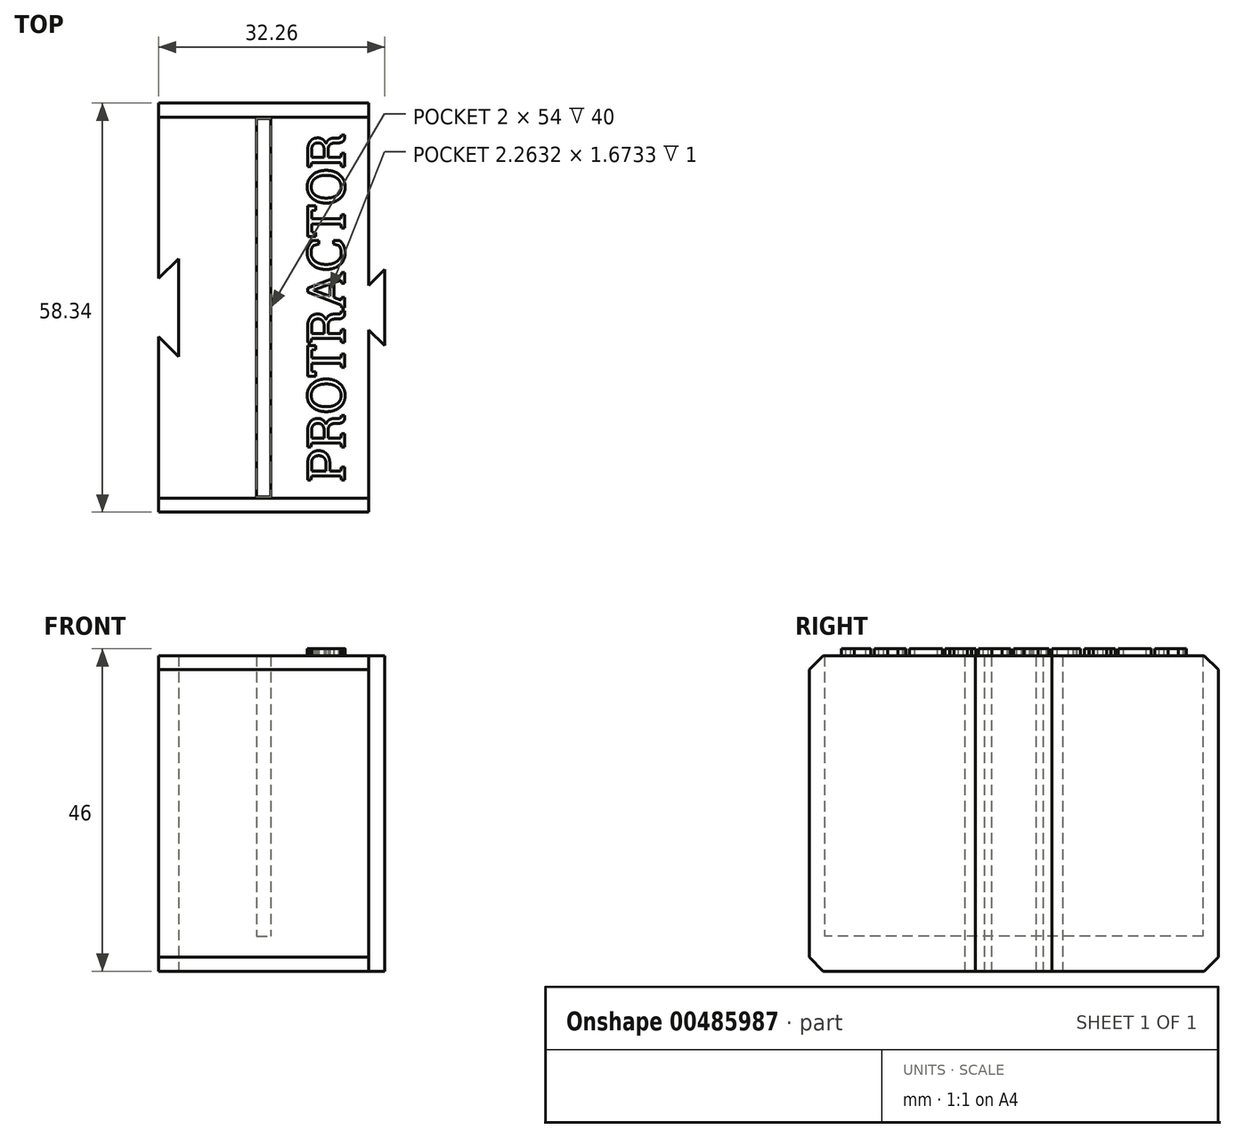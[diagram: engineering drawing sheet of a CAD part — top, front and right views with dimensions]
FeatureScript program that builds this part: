
annotation { "Feature Type Name" : "Feature", "Feature Type Description" : "" }
export const myFeature = defineFeature(function(context is Context, id is Id, definition is map)
    precondition{}
    {
        {
            var Q0;
            Q0=qCreatedBy(makeId("Top.planeOp"),FACE);
            var sketch = newSketch(context, id + "F0", { "sketchPlane" : qUnion([Q0])});
            skLineSegment(sketch, "E0", {"start": v(-15, 4.17) * mm, "end": v(-15, 29.17) * mm});
            skLineSegment(sketch, "E1", {"start": v(-15, 29.17) * mm, "end": v(15, 29.17) * mm});
            skLineSegment(sketch, "E2", {"start": v(15, 29.17) * mm, "end": v(15, 3.17) * mm});
            skLineSegment(sketch, "E3", {"start": v(-15, 4.17) * mm, "end": v(-12.17, 7) * mm});
            skLineSegment(sketch, "E4", {"start": v(-12.17, 7) * mm, "end": v(-12.17, 0) * mm});
            skLineSegment(sketch, "E5", {"start": v(15, 3.17) * mm, "end": v(17.26, 5.43) * mm});
            skLineSegment(sketch, "E6", {"start": v(17.26, 5.43) * mm, "end": v(17.26, -0.57) * mm});
            skLineSegment(sketch, "E7.MirrorCS", {"start": v(-15, -4.17) * mm, "end": v(-12.17, -7) * mm});
            skLineSegment(sketch, "E8.MirrorCS", {"start": v(15, -29.17) * mm, "end": v(15, -3.17) * mm});
            skLineSegment(sketch, "E9.MirrorCS", {"start": v(-12.17, -7) * mm, "end": v(-12.17, 0) * mm});
            skLineSegment(sketch, "E10.MirrorCS", {"start": v(-15, -4.17) * mm, "end": v(-15, -29.17) * mm});
            skLineSegment(sketch, "E11.MirrorCS", {"start": v(17.26, -5.43) * mm, "end": v(17.26, 0.57) * mm});
            skLineSegment(sketch, "E12.MirrorCS", {"start": v(15, -3.17) * mm, "end": v(17.26, -5.43) * mm});
            skLineSegment(sketch, "E13.MirrorCS", {"start": v(-15, -29.17) * mm, "end": v(15, -29.17) * mm});
            skLineSegment(sketch, "E14.bottom", {"start": v(-1, 27) * mm, "end": v(1, 27) * mm});
            skLineSegment(sketch, "E14.top", {"start": v(-1, -27) * mm, "end": v(1, -27) * mm});
            skLineSegment(sketch, "E14.left", {"start": v(-1, 27) * mm, "end": v(-1, -27) * mm});
            skLineSegment(sketch, "E14.right", {"start": v(1, 27) * mm, "end": v(1, -27) * mm});
            skPoint(sketch, "E14.middle", {"position": v(0, 0) * mm});
            skSolve(sketch);
        }
        {
            var Q0;
            Q0=qSketchRegion(id+"F0",true);
            extrude(context, id + "F1", {"entities" : qUnion([Q0]), "depth" : 40 * mm});
        }
        {
            var Q0;
            Q0=makeQuery(id+"F0.imprint","IMPRINT",FACE,{"disambiguationData":[TD([[makeQuery(id+"F0.imprint","IMPRINT",EDGE,{"derivedFrom":sQuery(id+"F0.wireOp",EDGE,"E0")}),-1.0]])]});
            var Q1;
            Q1=makeQuery(id+"F0.imprint","IMPRINT",FACE,{"disambiguationData":[TD([[makeQuery(id+"F0.imprint","IMPRINT",EDGE,{"derivedFrom":sQuery(id+"F0.wireOp",EDGE,"E14.bottom")}),-1.0]])]});
            extrude(context, id + "F2", {"entities" : qUnion([Q0, Q1]), "operationType" : NewBodyOperationType.ADD, "oppositeDirection" : true, "depth" : 5 * mm});
        }
        {
            var Q0;
            Q0=makeQuery(id+"F2.opExtrude","CAP_EDGE",EDGE,{"disambiguationData":[OSD([sQuery(id+"F0.wireOp",EDGE,"E13.MirrorCS")])],"isStart":false});
            var Q1;
            Q1=makeQuery(id+"F2.opExtrude","CAP_EDGE",EDGE,{"disambiguationData":[OSD([sQuery(id+"F0.wireOp",EDGE,"E1")])],"isStart":false});
            var Q2;
            Q2=makeQuery(id+"F1.opExtrude","CAP_EDGE",EDGE,{"disambiguationData":[OSD([sQuery(id+"F0.wireOp",EDGE,"E13.MirrorCS")])],"isStart":false});
            var Q3;
            Q3=makeQuery(id+"F1.opExtrude","CAP_EDGE",EDGE,{"disambiguationData":[OSD([sQuery(id+"F0.wireOp",EDGE,"E1")])],"isStart":false});
            chamfer(context, id + "F3", {"entities" : qUnion([Q0, Q1, Q2, Q3]), "width" : 2 * mm, "tangentPropagation" : true});
        }
        {
            var Q0;
            Q0=makeQuery(id+"F1.opExtrude","CAP_FACE",FACE,{"disambiguationData":[OSD([sQuery(id+"F0.wireOp",EDGE,"E0"),sQuery(id+"F0.wireOp",EDGE,"E1"),sQuery(id+"F0.wireOp",EDGE,"E2"),sQuery(id+"F0.wireOp",EDGE,"E3"),sQuery(id+"F0.wireOp",EDGE,"E4"),sQuery(id+"F0.wireOp",EDGE,"E5"),sQuery(id+"F0.wireOp",EDGE,"E6"),sQuery(id+"F0.wireOp",EDGE,"E7.MirrorCS"),sQuery(id+"F0.wireOp",EDGE,"E8.MirrorCS"),sQuery(id+"F0.wireOp",EDGE,"E9.MirrorCS"),sQuery(id+"F0.wireOp",EDGE,"E10.MirrorCS"),sQuery(id+"F0.wireOp",EDGE,"E11.MirrorCS"),sQuery(id+"F0.wireOp",EDGE,"E12.MirrorCS"),sQuery(id+"F0.wireOp",EDGE,"E13.MirrorCS"),sQuery(id+"F0.wireOp",EDGE,"E14.bottom"),sQuery(id+"F0.wireOp",EDGE,"E14.top"),sQuery(id+"F0.wireOp",EDGE,"E14.left"),sQuery(id+"F0.wireOp",EDGE,"E14.right")])],"isStart":false});
            var sketch = newSketch(context, id + "F4", { "sketchPlane" : qUnion([Q0])});
            skText(sketch, "E15", { "text": "PROTRACTOR", "fontName": "RobotoSlab-Regular.ttf"});
            const initialGuessF4  = {"E15": [0.01154, -0.02487, 0, 1, 0.00534]};
            skSetInitialGuess(sketch, initialGuessF4);
            skSolve(sketch);
        }
        {
            var Q0;
            Q0=qSketchRegion(id+"F4",true);
            extrude(context, id + "F5", {"entities" : qUnion([Q0]), "operationType" : NewBodyOperationType.ADD, "depth" : 1 * mm});
        }
    });
